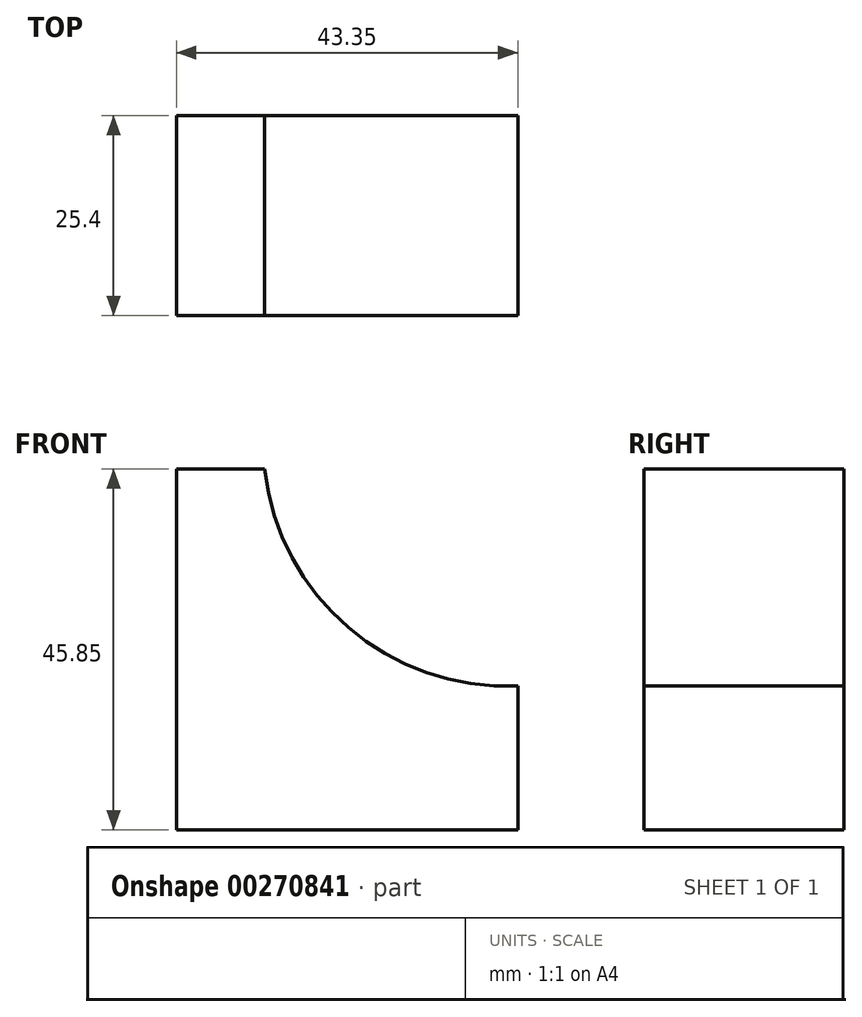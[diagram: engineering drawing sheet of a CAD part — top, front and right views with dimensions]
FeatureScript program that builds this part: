
annotation { "Feature Type Name" : "Feature", "Feature Type Description" : "" }
export const myFeature = defineFeature(function(context is Context, id is Id, definition is map)
    precondition{}
    {
        {
            var Q0;
            Q0=qCreatedBy(makeId("Front.planeOp"),FACE);
            var sketch = newSketch(context, id + "F0", { "sketchPlane" : qUnion([Q0])});
            skLineSegment(sketch, "E0", {"start": v(0, 0) * mm, "end": v(-43.35, 0) * mm});
            skLineSegment(sketch, "E1", {"start": v(-43.35, 0) * mm, "end": v(-43.35, 45.85) * mm});
            skLineSegment(sketch, "E2", {"start": v(-43.35, 45.85) * mm, "end": v(-32.16, 45.85) * mm});
            skArc(sketch, "E3", {"start": v(-32.16, 45.85) * mm, "mid": v(-21.52, 25.72) * mm, "end": v(0, 18.28) * mm});
            skLineSegment(sketch, "E4", {"start": v(0, 18.28) * mm, "end": v(0, 0) * mm});
            skSolve(sketch);
        }
        {
            var Q0;
            Q0 = qSketchRegion(id + "F0", true);
            extrude(context, id + "F1", {"entities" : qUnion([Q0]), "depth" : 25.4 * mm});
        }
    });
